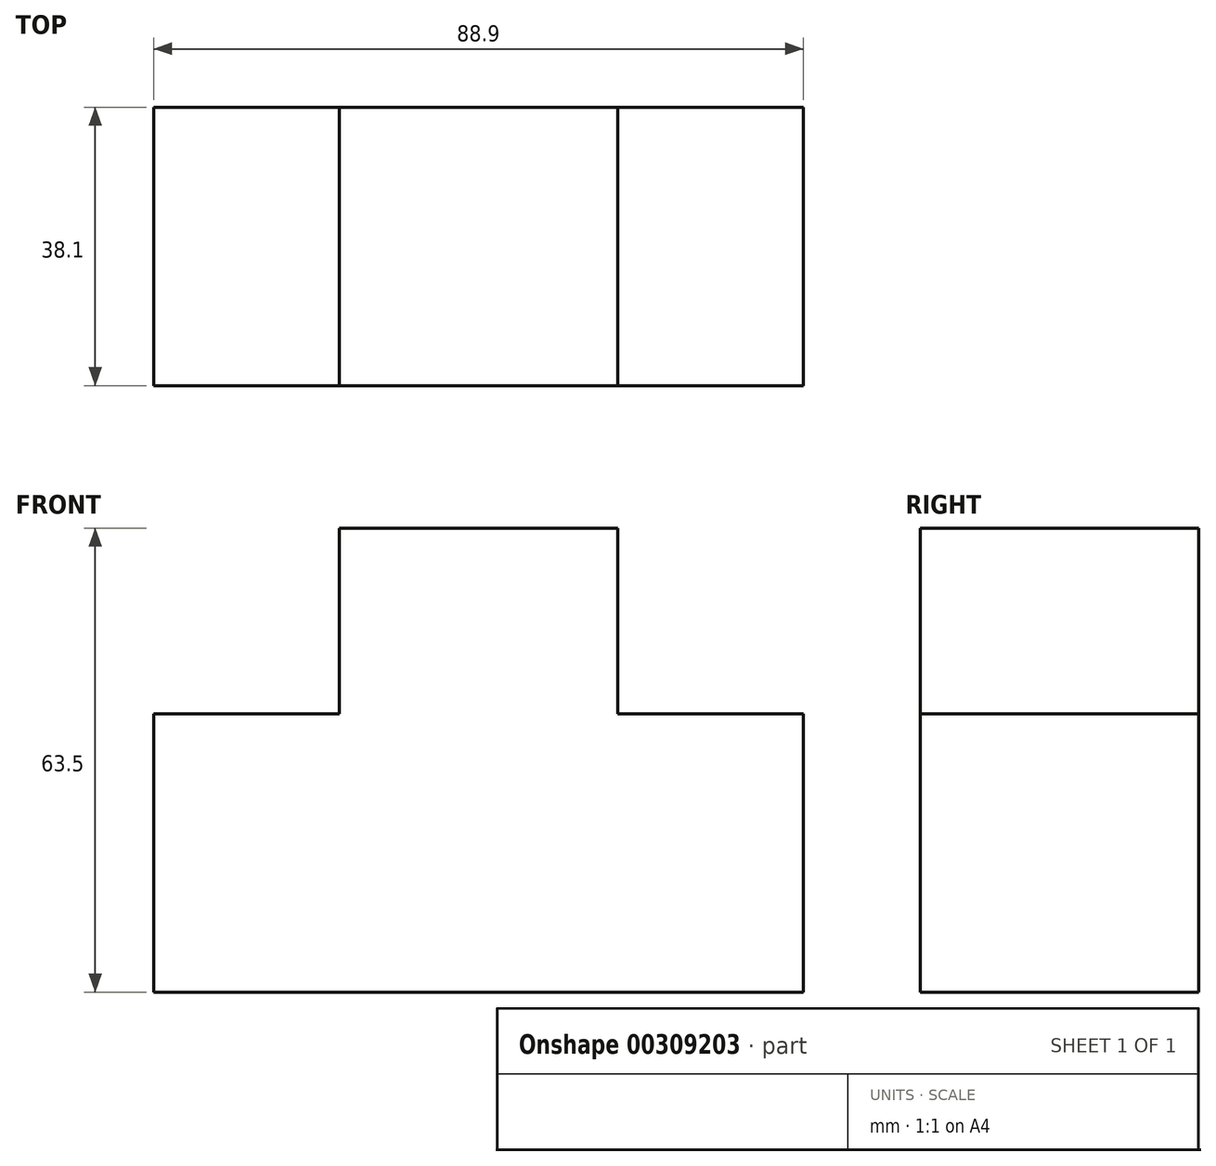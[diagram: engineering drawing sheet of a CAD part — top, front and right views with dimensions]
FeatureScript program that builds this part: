
annotation { "Feature Type Name" : "Feature", "Feature Type Description" : "" }
export const myFeature = defineFeature(function(context is Context, id is Id, definition is map)
    precondition{}
    {
        {
            var Q0;
            Q0=qCreatedBy(makeId("Front.planeOp"),FACE);
            var sketch = newSketch(context, id + "F0", { "sketchPlane" : qUnion([Q0])});
            skLineSegment(sketch, "E0", {"start": v(-45.36, -41.47) * mm, "end": v(43.54, -41.47) * mm});
            skLineSegment(sketch, "E1", {"start": v(43.54, -41.47) * mm, "end": v(43.54, -3.37) * mm});
            skLineSegment(sketch, "E2", {"start": v(43.54, -3.37) * mm, "end": v(18.14, -3.37) * mm});
            skLineSegment(sketch, "E3", {"start": v(18.14, -3.37) * mm, "end": v(18.14, 22.03) * mm});
            skLineSegment(sketch, "E4", {"start": v(18.14, 22.03) * mm, "end": v(-19.96, 22.03) * mm});
            skLineSegment(sketch, "E5", {"start": v(-19.96, 22.03) * mm, "end": v(-19.96, -3.37) * mm});
            skLineSegment(sketch, "E6", {"start": v(-19.96, -3.37) * mm, "end": v(-45.36, -3.37) * mm});
            skLineSegment(sketch, "E7", {"start": v(-45.36, -3.37) * mm, "end": v(-45.36, -41.47) * mm});
            skSolve(sketch);
        }
        {
            var Q0;
            Q0=makeQuery(id+"F0.imprint","IMPRINT",FACE,{"disambiguationData":[TD([[makeQuery(id+"F0.imprint","IMPRINT",EDGE,{"derivedFrom":sQuery(id+"F0.wireOp",EDGE,"E0")}),1.0]])]});
            extrude(context, id + "F1", {"entities" : qUnion([Q0]), "depth" : 38.1 * mm});
        }
    });
